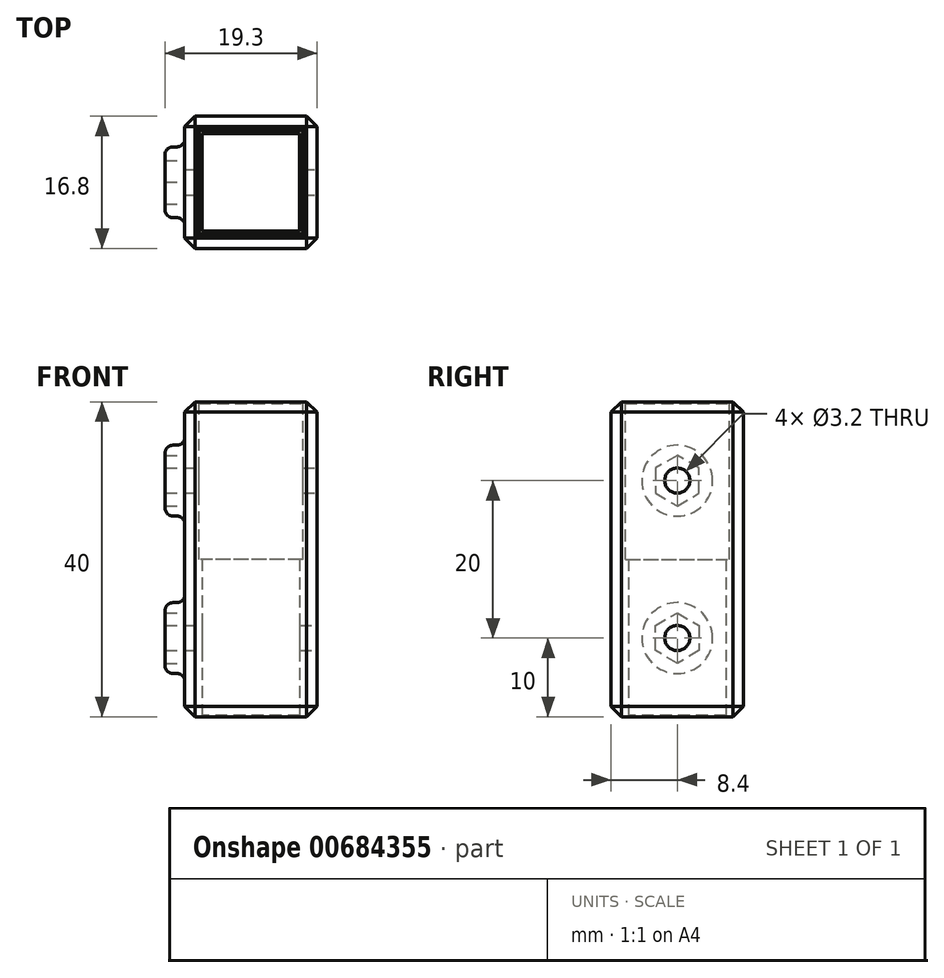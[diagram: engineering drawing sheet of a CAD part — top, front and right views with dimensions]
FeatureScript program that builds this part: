
annotation { "Feature Type Name" : "Feature", "Feature Type Description" : "" }
export const myFeature = defineFeature(function(context is Context, id is Id, definition is map)
    precondition{}
    {
        {
            var Q0;
            Q0=qCreatedBy(makeId("Top.planeOp"),FACE);
            var sketch = newSketch(context, id + "F0", { "sketchPlane" : qUnion([Q0])});
            skLineSegment(sketch, "E0.bottom", {"start": v(6.2, -6.2) * mm, "end": v(-6.2, -6.2) * mm});
            skLineSegment(sketch, "E0.top", {"start": v(6.2, 6.2) * mm, "end": v(-6.2, 6.2) * mm});
            skLineSegment(sketch, "E0.left", {"start": v(6.2, -6.2) * mm, "end": v(6.2, 6.2) * mm});
            skLineSegment(sketch, "E0.right", {"start": v(-6.2, -6.2) * mm, "end": v(-6.2, 6.2) * mm});
            skPoint(sketch, "E0.middle", {"position": v(0, 0) * mm});
            skLineSegment(sketch, "E1.0", {"start": v(8.4, 8.4) * mm, "end": v(-8.4, 8.4) * mm});
            skLineSegment(sketch, "E1.1", {"start": v(8.4, -8.4) * mm, "end": v(8.4, 8.4) * mm});
            skLineSegment(sketch, "E1.2", {"start": v(8.4, -8.4) * mm, "end": v(-8.4, -8.4) * mm});
            skLineSegment(sketch, "E1.3", {"start": v(-8.4, -8.4) * mm, "end": v(-8.4, 8.4) * mm});
            skSolve(sketch);
        }
        {
            var Q0;
            Q0=qCreatedBy(makeId("Top.planeOp"),FACE);
            cPlane(context, id + "F1", {"entities" : qUnion([Q0]), "cplaneType" : CPlaneType.OFFSET, "offset" : 40 * mm, "width" : 150 * mm, "height" : 150 * mm});
        }
        {
            var Q0;
            Q0=qCreatedBy(id+"F1.planeOp",FACE);
            var sketch = newSketch(context, id + "F2", { "sketchPlane" : qUnion([Q0])});
            skLineSegment(sketch, "E2.bottom", {"start": v(6.6, -6.6) * mm, "end": v(-6.6, -6.6) * mm});
            skLineSegment(sketch, "E2.top", {"start": v(6.6, 6.6) * mm, "end": v(-6.6, 6.6) * mm});
            skLineSegment(sketch, "E2.left", {"start": v(6.6, -6.6) * mm, "end": v(6.6, 6.6) * mm});
            skLineSegment(sketch, "E2.right", {"start": v(-6.6, -6.6) * mm, "end": v(-6.6, 6.6) * mm});
            skPoint(sketch, "E2.middle", {"position": v(0, 0) * mm});
            skLineSegment(sketch, "E3.0", {"start": v(-8.4, -8.4) * mm, "end": v(-8.4, 8.4) * mm});
            skLineSegment(sketch, "E3.1", {"start": v(8.4, -8.4) * mm, "end": v(-8.4, -8.4) * mm});
            skLineSegment(sketch, "E3.2", {"start": v(8.4, -8.4) * mm, "end": v(8.4, 8.4) * mm});
            skLineSegment(sketch, "E3.3", {"start": v(8.4, 8.4) * mm, "end": v(-8.4, 8.4) * mm});
            skSolve(sketch);
        }
        {
            var Q0;
            Q0=makeQuery(id+"F0.imprint","IMPRINT",FACE,{"disambiguationData":[TD([[makeQuery(id+"F0.imprint","IMPRINT",EDGE,{"derivedFrom":sQuery(id+"F0.wireOp",EDGE,"E0.bottom")}),1.0]])]});
            extrude(context, id + "F3", {"entities" : qUnion([Q0]), "depth" : 20 * mm, "offsetDistance" : 25 * mm});
        }
        {
            var Q0;
            Q0=makeQuery(id+"F2.imprint","IMPRINT",FACE,{"disambiguationData":[TD([[makeQuery(id+"F2.imprint","IMPRINT",EDGE,{"derivedFrom":sQuery(id+"F2.wireOp",EDGE,"E2.bottom")}),1.0]])]});
            extrude(context, id + "F4", {"entities" : qUnion([Q0]), "operationType" : NewBodyOperationType.ADD, "oppositeDirection" : true, "depth" : 20 * mm, "offsetDistance" : 25 * mm});
        }
        {
            var Q0;
            Q0=makeQuery(id+"F4.boolean.opBoolean","MERGE",FACE,{"derivedFrom":[makeQuery(id+"F3.opExtrude","SWEPT_FACE",FACE,{"disambiguationData":[OSD([sQuery(id+"F0.wireOp",EDGE,"E1.1")])]}),makeQuery(id+"F4.opExtrude","SWEPT_FACE",FACE,{"disambiguationData":[OSD([sQuery(id+"F2.wireOp",EDGE,"E3.2")])]})]});
            var sketch = newSketch(context, id + "F5", { "sketchPlane" : qUnion([Q0])});
            skCircle(sketch, "E4", {"center": v(0, 30) * mm, "radius": 1.6 * mm});
            skCircle(sketch, "E5", {"center": v(0, 10) * mm, "radius": 1.6 * mm});
            skSolve(sketch);
        }
        {
            var Q0;
            Q0 = qSketchRegion(id + "F5", true);
            extrude(context, id + "F6", {"entities" : qUnion([Q0]), "operationType" : NewBodyOperationType.REMOVE, "oppositeDirection" : true, "depth" : 25 * mm, "offsetDistance" : 25 * mm});
        }
        {
            var Q0;
            Q0=makeQuery(id+"F4.boolean.opBoolean","MERGE",FACE,{"derivedFrom":[makeQuery(id+"F3.opExtrude","SWEPT_FACE",FACE,{"disambiguationData":[OSD([sQuery(id+"F0.wireOp",EDGE,"E1.3")])]}),makeQuery(id+"F4.opExtrude","SWEPT_FACE",FACE,{"disambiguationData":[OSD([sQuery(id+"F2.wireOp",EDGE,"E3.0")])]})]});
            var sketch = newSketch(context, id + "F7", { "sketchPlane" : qUnion([Q0])});
            skCircle(sketch, "E6.cCircle", {"center": v(0, 30) * mm, "radius": 2.77 * mm, "construction": true});
            skLineSegment(sketch, "E6.0", {"start": v(2.77, 31.6) * mm, "end": v(2.77, 28.4) * mm});
            skLineSegment(sketch, "E6.1", {"start": v(2.77, 28.4) * mm, "end": v(0, 26.8) * mm});
            skLineSegment(sketch, "E6.2", {"start": v(0, 26.8) * mm, "end": v(-2.77, 28.4) * mm});
            skLineSegment(sketch, "E6.3", {"start": v(-2.77, 28.4) * mm, "end": v(-2.77, 31.6) * mm});
            skLineSegment(sketch, "E6.4", {"start": v(-2.77, 31.6) * mm, "end": v(0, 33.2) * mm});
            skLineSegment(sketch, "E6.5", {"start": v(0, 33.2) * mm, "end": v(2.77, 31.6) * mm});
            skPoint(sketch, "E6.0.midPoint", {"position": v(2.77, 30) * mm});
            skCircle(sketch, "E7", {"center": v(0, 30) * mm, "radius": 4.5 * mm});
            skLineSegment(sketch, "E8", {"start": v(0, 40) * mm, "end": v(0, 20) * mm, "construction": true});
            skLineSegment(sketch, "E9", {"start": v(0, 20) * mm, "end": v(-6.37, 20) * mm, "construction": true});
            skLineSegment(sketch, "E10.MirrorCS", {"start": v(2.77, 11.6) * mm, "end": v(0, 13.2) * mm});
            skLineSegment(sketch, "E11.MirrorCS", {"start": v(0, 13.2) * mm, "end": v(-2.77, 11.6) * mm});
            skPoint(sketch, "E12.MirrorP", {"position": v(2.77, 10) * mm});
            skCircle(sketch, "E13.MirrorC", {"center": v(0, 10) * mm, "radius": 4.5 * mm});
            skLineSegment(sketch, "E14.MirrorCS", {"start": v(0, 6.8) * mm, "end": v(2.77, 8.4) * mm});
            skLineSegment(sketch, "E15.MirrorCS", {"start": v(-2.77, 8.4) * mm, "end": v(0, 6.8) * mm});
            skCircle(sketch, "E16.MirrorC", {"center": v(0, 10) * mm, "radius": 2.77 * mm, "construction": true});
            skLineSegment(sketch, "E17.MirrorCS", {"start": v(2.77, 8.4) * mm, "end": v(2.77, 11.6) * mm});
            skLineSegment(sketch, "E18.MirrorCS", {"start": v(-2.77, 11.6) * mm, "end": v(-2.77, 8.4) * mm});
            skSolve(sketch);
        }
        {
            var Q0;
            Q0=makeQuery(id+"F7.imprint","IMPRINT",FACE,{"disambiguationData":[TD([[makeQuery(id+"F7.imprint","IMPRINT",EDGE,{"derivedFrom":sQuery(id+"F7.wireOp",EDGE,"E10.MirrorCS")}),-1.0]])]});
            var Q1;
            Q1=makeQuery(id+"F7.imprint","IMPRINT",FACE,{"disambiguationData":[TD([[makeQuery(id+"F7.imprint","IMPRINT",EDGE,{"derivedFrom":sQuery(id+"F7.wireOp",EDGE,"E6.0")}),1.0]])]});
            extrude(context, id + "F8", {"entities" : qUnion([Q0, Q1]), "operationType" : NewBodyOperationType.ADD, "depth" : 2.5 * mm, "offsetDistance" : 25 * mm});
        }
        {
            var Q0;
            Q0=makeQuery(id+"F4.opExtrude","CAP_EDGE",EDGE,{"disambiguationData":[OSD([sQuery(id+"F2.wireOp",EDGE,"E2.top")])],"isStart":true});
            var Q1;
            Q1=makeQuery(id+"F4.opExtrude","CAP_EDGE",EDGE,{"disambiguationData":[OSD([sQuery(id+"F2.wireOp",EDGE,"E2.right")])],"isStart":true});
            var Q2;
            Q2=makeQuery(id+"F4.opExtrude","CAP_EDGE",EDGE,{"disambiguationData":[OSD([sQuery(id+"F2.wireOp",EDGE,"E2.bottom")])],"isStart":true});
            var Q3;
            Q3=makeQuery(id+"F4.opExtrude","CAP_EDGE",EDGE,{"disambiguationData":[OSD([sQuery(id+"F2.wireOp",EDGE,"E2.left")])],"isStart":true});
            var Q4;
            Q4=makeQuery(id+"F3.opExtrude","CAP_EDGE",EDGE,{"disambiguationData":[OSD([sQuery(id+"F0.wireOp",EDGE,"E0.bottom")])],"isStart":true});
            var Q5;
            Q5=makeQuery(id+"F3.opExtrude","CAP_EDGE",EDGE,{"disambiguationData":[OSD([sQuery(id+"F0.wireOp",EDGE,"E0.left")])],"isStart":true});
            var Q6;
            Q6=makeQuery(id+"F3.opExtrude","CAP_EDGE",EDGE,{"disambiguationData":[OSD([sQuery(id+"F0.wireOp",EDGE,"E0.top")])],"isStart":true});
            var Q7;
            Q7=makeQuery(id+"F3.opExtrude","CAP_EDGE",EDGE,{"disambiguationData":[OSD([sQuery(id+"F0.wireOp",EDGE,"E0.right")])],"isStart":true});
            chamfer(context, id + "F9", {"entities" : qUnion([Q0, Q1, Q2, Q3, Q4, Q5, Q6, Q7]), "width" : 0.2 * mm, "tangentPropagation" : true});
        }
        {
            var Q0;
            Q0=makeQuery(id+"F8.opExtrude","CAP_EDGE",EDGE,{"disambiguationData":[OSD([sQuery(id+"F7.wireOp",EDGE,"E13.MirrorC")])],"isStart":true});
            var Q1;
            Q1=makeQuery(id+"F8.opExtrude","CAP_EDGE",EDGE,{"disambiguationData":[OSD([sQuery(id+"F7.wireOp",EDGE,"E13.MirrorC")])],"isStart":false});
            var Q2;
            Q2=makeQuery(id+"F8.opExtrude","CAP_EDGE",EDGE,{"disambiguationData":[OSD([sQuery(id+"F7.wireOp",EDGE,"E7")])],"isStart":false});
            var Q3;
            Q3=makeQuery(id+"F8.opExtrude","CAP_EDGE",EDGE,{"disambiguationData":[OSD([sQuery(id+"F7.wireOp",EDGE,"E7")])],"isStart":true});
            fillet(context, id + "F10", {"entities" : qUnion([Q0, Q1, Q2, Q3]), "radius" : 1 * mm, "tangentPropagation" : true, "allowEdgeOverflow" : false});
        }
        {
            var Q0;
            Q0=makeQuery(id+"F4.boolean.opBoolean","MERGE",FACE,{"derivedFrom":[makeQuery(id+"F3.opExtrude","SWEPT_FACE",FACE,{"disambiguationData":[OSD([sQuery(id+"F0.wireOp",EDGE,"E1.0")])]}),makeQuery(id+"F4.opExtrude","SWEPT_FACE",FACE,{"disambiguationData":[OSD([sQuery(id+"F2.wireOp",EDGE,"E3.3")])]})]});
            var Q1;
            Q1=makeQuery(id+"F4.boolean.opBoolean","MERGE",FACE,{"derivedFrom":[makeQuery(id+"F3.opExtrude","SWEPT_FACE",FACE,{"disambiguationData":[OSD([sQuery(id+"F0.wireOp",EDGE,"E1.2")])]}),makeQuery(id+"F4.opExtrude","SWEPT_FACE",FACE,{"disambiguationData":[OSD([sQuery(id+"F2.wireOp",EDGE,"E3.1")])]})]});
            var Q2;
            Q2=makeQuery(id+"F3.opExtrude","CAP_EDGE",EDGE,{"disambiguationData":[OSD([sQuery(id+"F0.wireOp",EDGE,"E1.1")])],"isStart":true});
            var Q3;
            Q3=makeQuery(id+"F3.opExtrude","CAP_EDGE",EDGE,{"disambiguationData":[OSD([sQuery(id+"F0.wireOp",EDGE,"E1.3")])],"isStart":true});
            var Q4;
            Q4=makeQuery(id+"F4.opExtrude","CAP_EDGE",EDGE,{"disambiguationData":[OSD([sQuery(id+"F2.wireOp",EDGE,"E3.0")])],"isStart":true});
            var Q5;
            Q5=makeQuery(id+"F4.opExtrude","CAP_EDGE",EDGE,{"disambiguationData":[OSD([sQuery(id+"F2.wireOp",EDGE,"E3.2")])],"isStart":true});
            chamfer(context, id + "F11", {"entities" : qUnion([Q0, Q1, Q2, Q3, Q4, Q5]), "width" : 1.3 * mm, "tangentPropagation" : true});
        }
    });
